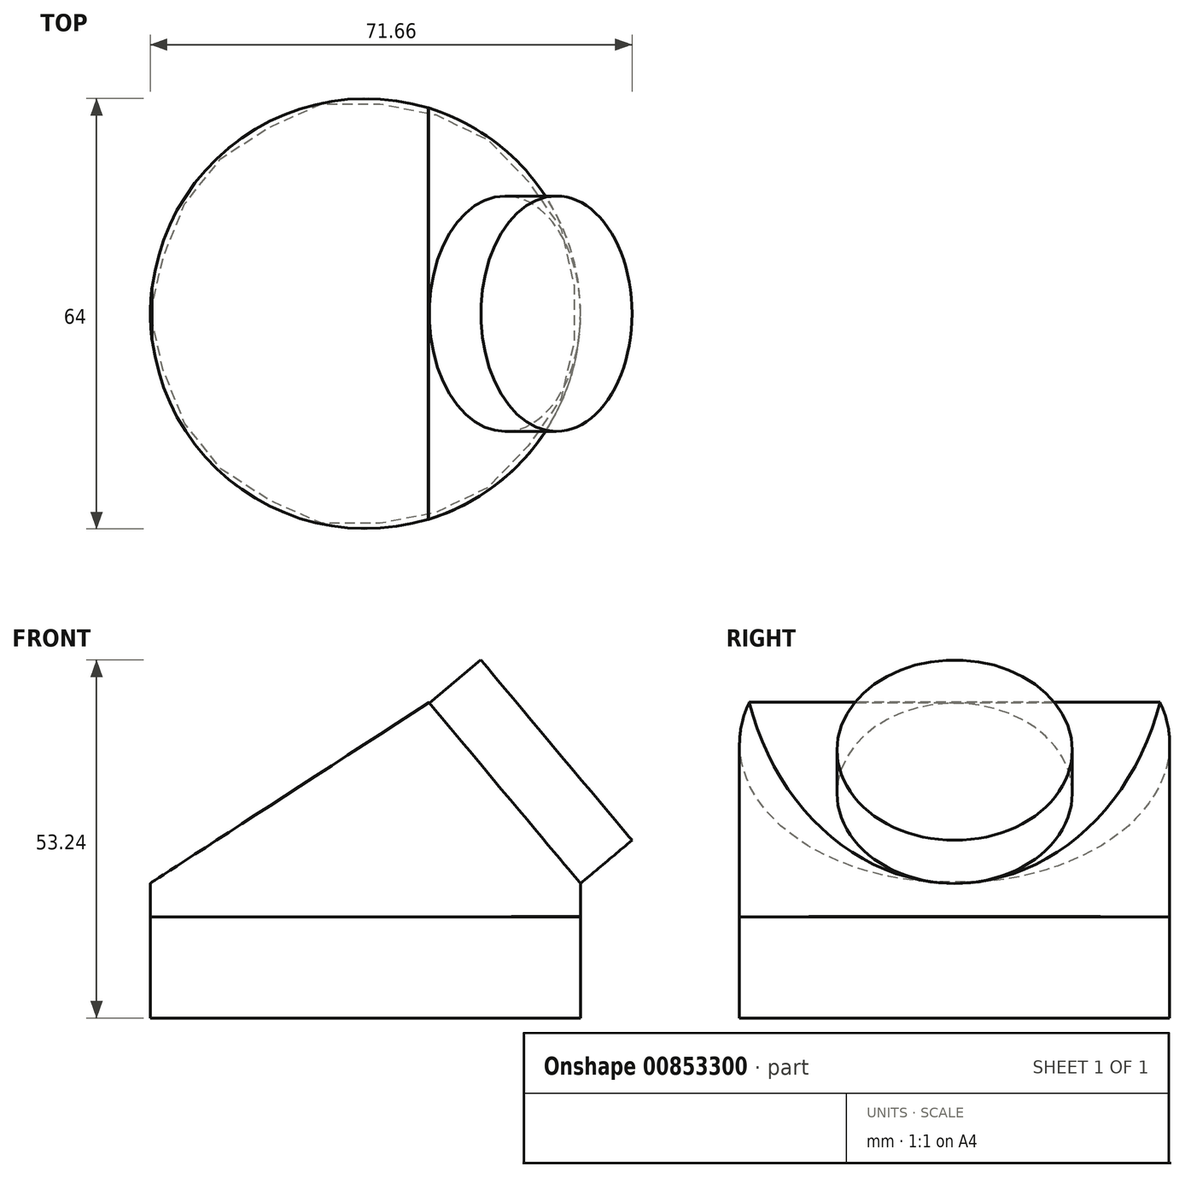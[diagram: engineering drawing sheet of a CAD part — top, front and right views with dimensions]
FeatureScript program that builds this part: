
annotation { "Feature Type Name" : "Feature", "Feature Type Description" : "" }
export const myFeature = defineFeature(function(context is Context, id is Id, definition is map)
    precondition{}
    {
        {
            var Q0;
            Q0=qCreatedBy(makeId("Top.planeOp"),FACE);
            var sketch = newSketch(context, id + "F0", { "sketchPlane" : qUnion([Q0])});
            skCircle(sketch, "E0", {"center": v(0, 0) * mm, "radius": 32 * mm});
            skSolve(sketch);
        }
        {
            var Q0;
            Q0=makeQuery(id+"F0.imprint","IMPRINT",FACE,{"disambiguationData":[TD([[makeQuery(id+"F0.imprint","IMPRINT",EDGE,{"derivedFrom":sQuery(id+"F0.wireOp",EDGE,"E0")}),1.0]])]});
            extrude(context, id + "F1", {"entities" : qUnion([Q0]), "depth" : 15 * mm, "offsetDistance" : 25 * mm});
        }
        {
            var Q0;
            Q0=qCreatedBy(makeId("Front.planeOp"),FACE);
            var sketch = newSketch(context, id + "F2", { "sketchPlane" : qUnion([Q0])});
            skLineSegment(sketch, "E1", {"start": v(32, 20) * mm, "end": v(9.5, 46.81) * mm});
            skLineSegment(sketch, "E2", {"start": v(32, 20) * mm, "end": v(-32, 20) * mm});
            skLineSegment(sketch, "E3", {"start": v(32, 20) * mm, "end": v(32, 15.07) * mm});
            skPoint(sketch, "E4", {"position": v(20.75, 33.4) * mm});
            skLineSegment(sketch, "E5", {"start": v(-32, 20) * mm, "end": v(14.2, 58.76) * mm});
            skLineSegment(sketch, "E6", {"start": v(9.5, 46.81) * mm, "end": v(5.56, 51.51) * mm});
            skLineSegment(sketch, "E7", {"start": v(-32, 20) * mm, "end": v(-32, 15) * mm});
            skLineSegment(sketch, "E8", {"start": v(-32, 15) * mm, "end": v(32, 15.07) * mm});
            skSolve(sketch);
        }
        {
            var Q0;
            Q0=makeQuery(id+"F2.imprint","IMPRINT",FACE,{"disambiguationData":[TD([[makeQuery(id+"F2.imprint","IMPRINT",EDGE,{"derivedFrom":sQuery(id+"F2.wireOp",EDGE,"E2")}),1.0]])]});
            var Q1;
            Q1=makeQuery(id+"F2.imprint","IMPRINT",FACE,{"disambiguationData":[TD([[makeQuery(id+"F2.imprint","IMPRINT",EDGE,{"derivedFrom":sQuery(id+"F2.wireOp",EDGE,"E1")}),1.0]])]});
            extrude(context, id + "F3", {"entities" : qUnion([Q0, Q1]), "endBound" : BoundingType.SYMMETRIC, "oppositeDirection" : true, "depth" : 64 * mm, "offsetDistance" : 25 * mm});
        }
        {
            var Q0;
            Q0=makeQuery(id+"F1.opExtrude","CAP_FACE",FACE,{"disambiguationData":[OSD([sQuery(id+"F0.wireOp",EDGE,"E0")])],"isStart":true});
            var sketch = newSketch(context, id + "F4", { "sketchPlane" : qUnion([Q0])});
            skCircle(sketch, "E9", {"center": v(0, 0) * mm, "radius": 32 * mm});
            skCircle(sketch, "E10", {"center": v(0, 0) * mm, "radius": 50 * mm});
            skSolve(sketch);
        }
        {
            var Q0;
            Q0=makeQuery(id+"F4.imprint","IMPRINT",FACE,{"disambiguationData":[TD([[makeQuery(id+"F4.imprint","IMPRINT",EDGE,{"derivedFrom":sQuery(id+"F4.wireOp",EDGE,"E9")}),1.0]])]});
            extrude(context, id + "F5", {"entities" : qUnion([Q0]), "operationType" : NewBodyOperationType.REMOVE, "oppositeDirection" : true, "depth" : 50 * mm, "offsetDistance" : 25 * mm});
        }
        {
            var Q0;
            Q0=makeQuery(id+"F3.opExtrude","SWEPT_FACE",FACE,{"disambiguationData":[OSD([sQuery(id+"F2.wireOp",EDGE,"E1"),sQuery(id+"F2.wireOp",EDGE,"E6")])]});
            var sketch = newSketch(context, id + "F6", { "sketchPlane" : qUnion([Q0])});
            skCircle(sketch, "E11", {"center": v(0, 12.25) * mm, "radius": 17.5 * mm});
            skSolve(sketch);
        }
        {
            var Q0;
            Q0=makeQuery(id+"F6.imprint","IMPRINT",FACE,{"disambiguationData":[TD([[makeQuery(id+"F6.imprint","IMPRINT",EDGE,{"derivedFrom":sQuery(id+"F6.wireOp",EDGE,"E11")}),1.0]])]});
            extrude(context, id + "F7", {"entities" : qUnion([Q0]), "operationType" : NewBodyOperationType.ADD, "depth" : 10 * mm, "offsetDistance" : 25 * mm});
        }
        {
            var Q0;
            Q0=qCreatedBy(makeId("Front.planeOp"),FACE);
            var sketch = newSketch(context, id + "F8", { "sketchPlane" : qUnion([Q0])});
            skLineSegment(sketch, "E12", {"start": v(9.36, 46.87) * mm, "end": v(-34.37, 18.5) * mm});
            skLineSegment(sketch, "E13", {"start": v(-34.37, 18.5) * mm, "end": v(-32.18, 40.37) * mm});
            skLineSegment(sketch, "E14", {"start": v(-32.18, 40.37) * mm, "end": v(10.33, 58.12) * mm});
            skLineSegment(sketch, "E15", {"start": v(10.33, 58.12) * mm, "end": v(9.36, 46.87) * mm});
            skSolve(sketch);
        }
        {
            var Q0;
            Q0=makeQuery(id+"F8.imprint","IMPRINT",FACE,{"disambiguationData":[TD([[makeQuery(id+"F8.imprint","IMPRINT",EDGE,{"derivedFrom":sQuery(id+"F8.wireOp",EDGE,"E12")}),-1.0]])]});
            extrude(context, id + "F9", {"entities" : qUnion([Q0]), "operationType" : NewBodyOperationType.REMOVE, "endBound" : BoundingType.SYMMETRIC, "oppositeDirection" : true, "depth" : 64 * mm, "offsetDistance" : 25 * mm});
        }
    });
